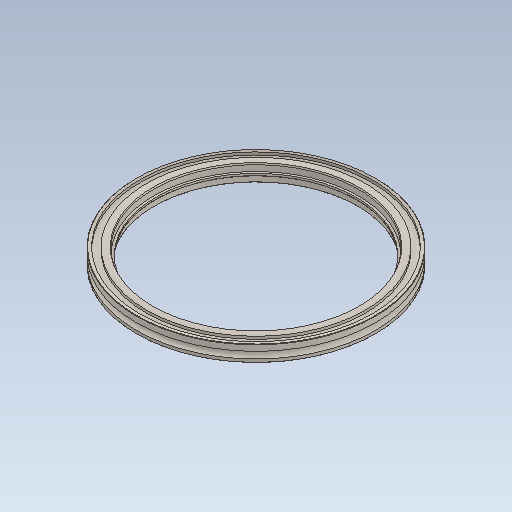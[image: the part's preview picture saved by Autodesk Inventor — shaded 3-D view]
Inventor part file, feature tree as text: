
AUTODESK INVENTOR PART (.ipt)
format: ipt  version: 2021 (Build 250183000, 183)  size: 185,856 bytes
history: native  units: in
note: dims shown in document units (in); Inventor stores cm internally (conversion verified against a paired STEP export)
features: fillet x1
ambient origin geometry x8: Origin, YZ Plane, XZ Plane, XY Plane, X Axis, Y Axis, Z Axis, Center Point
bodies: Solid1 (feature_tree)
feature tree (1):
  fillet  "Fillet1"  [1 undecoded]
note: 1 required parameter value undecoded (feature->parameter linkage not recoverable at this tier; creation-order binding heuristic only, values carry confidence <= 0.55)
